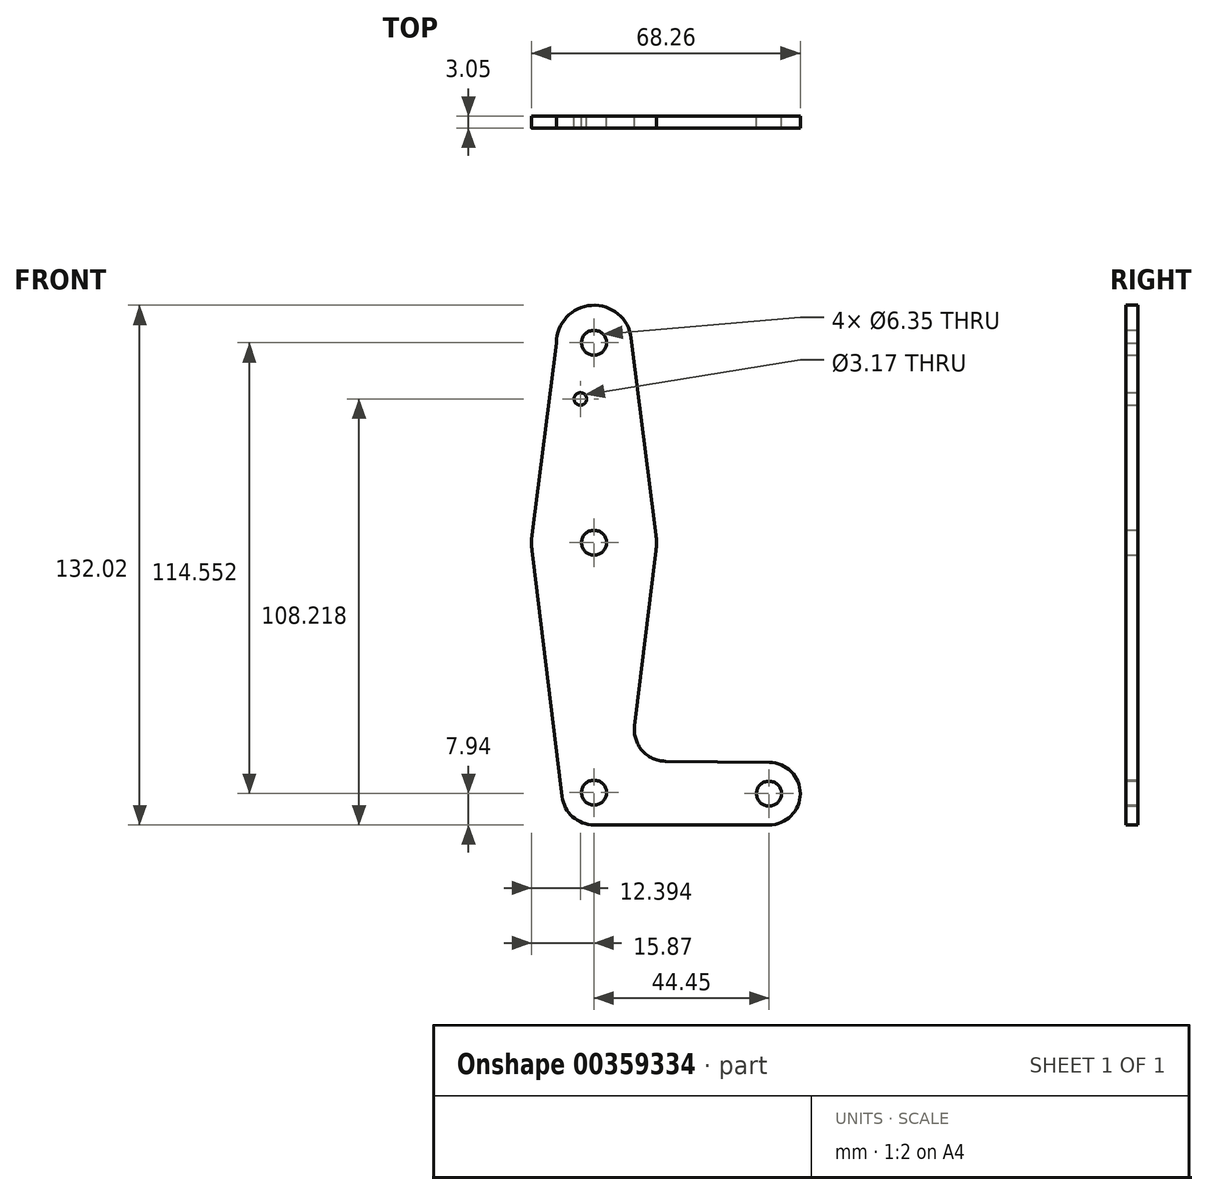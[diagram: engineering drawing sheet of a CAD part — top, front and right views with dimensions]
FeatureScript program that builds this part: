
annotation { "Feature Type Name" : "Feature", "Feature Type Description" : "" }
export const myFeature = defineFeature(function(context is Context, id is Id, definition is map)
    precondition{}
    {
        {
            var Q0;
            Q0=qCreatedBy(makeId("Front.planeOp"),FACE);
            var sketch = newSketch(context, id + "F0", { "sketchPlane" : qUnion([Q0])});
            skCircle(sketch, "E0", {"center": v(0, 83.31) * mm, "radius": 9.53 * mm});
            skCircle(sketch, "E1", {"center": v(0, 32.51) * mm, "radius": 15.88 * mm});
            skCircle(sketch, "E2", {"center": v(0, -30.99) * mm, "radius": 8.19 * mm});
            skCircle(sketch, "E3", {"center": v(44.45, -31.24) * mm, "radius": 7.94 * mm});
            skLineSegment(sketch, "E4", {"start": v(0, 83.31) * mm, "end": v(0, -30.99) * mm, "construction": true});
            skLineSegment(sketch, "E5", {"start": v(0, -30.99) * mm, "end": v(44.45, -31.24) * mm, "construction": true});
            skLineSegment(sketch, "E6", {"start": v(-9.52, 83.26) * mm, "end": v(-15.75, 34.52) * mm});
            skLineSegment(sketch, "E7", {"start": v(-15.75, 34.52) * mm, "end": v(-15.75, 30.5) * mm});
            skLineSegment(sketch, "E8", {"start": v(-15.75, 30.5) * mm, "end": v(-8.13, -31.98) * mm});
            skLineSegment(sketch, "E9", {"start": v(9.45, 84.5) * mm, "end": v(15.75, 34.5) * mm});
            skLineSegment(sketch, "E10", {"start": v(15.75, 34.5) * mm, "end": v(15.75, 30.53) * mm});
            skLineSegment(sketch, "E11", {"start": v(15.75, 30.53) * mm, "end": v(10.31, -14.1) * mm});
            skLineSegment(sketch, "E12", {"start": v(18.11, -23) * mm, "end": v(44.54, -23.3) * mm});
            skLineSegment(sketch, "E13", {"start": v(0, -39.18) * mm, "end": v(44.45, -39.18) * mm});
            skCircle(sketch, "E14", {"center": v(0, 83.31) * mm, "radius": 3.18 * mm});
            skCircle(sketch, "E15", {"center": v(-3.48, 69.04) * mm, "radius": 1.59 * mm});
            skCircle(sketch, "E16", {"center": v(0, 32.51) * mm, "radius": 3.18 * mm});
            skCircle(sketch, "E17", {"center": v(0, -30.99) * mm, "radius": 3.18 * mm});
            skCircle(sketch, "E18", {"center": v(44.45, -31.24) * mm, "radius": 3.18 * mm});
            skArc(sketch, "E19.filletArc", {"start": v(10.31, -14.1) * mm, "mid": v(12.22, -20.3) * mm, "end": v(18.11, -23) * mm});
            skSolve(sketch);
        }
        {
            var Q0;
            Q0 = qSketchRegion(id + "F0", true);
            extrude(context, id + "F1", {"entities" : qUnion([Q0]), "depth" : 3.05 * mm});
        }
    });
